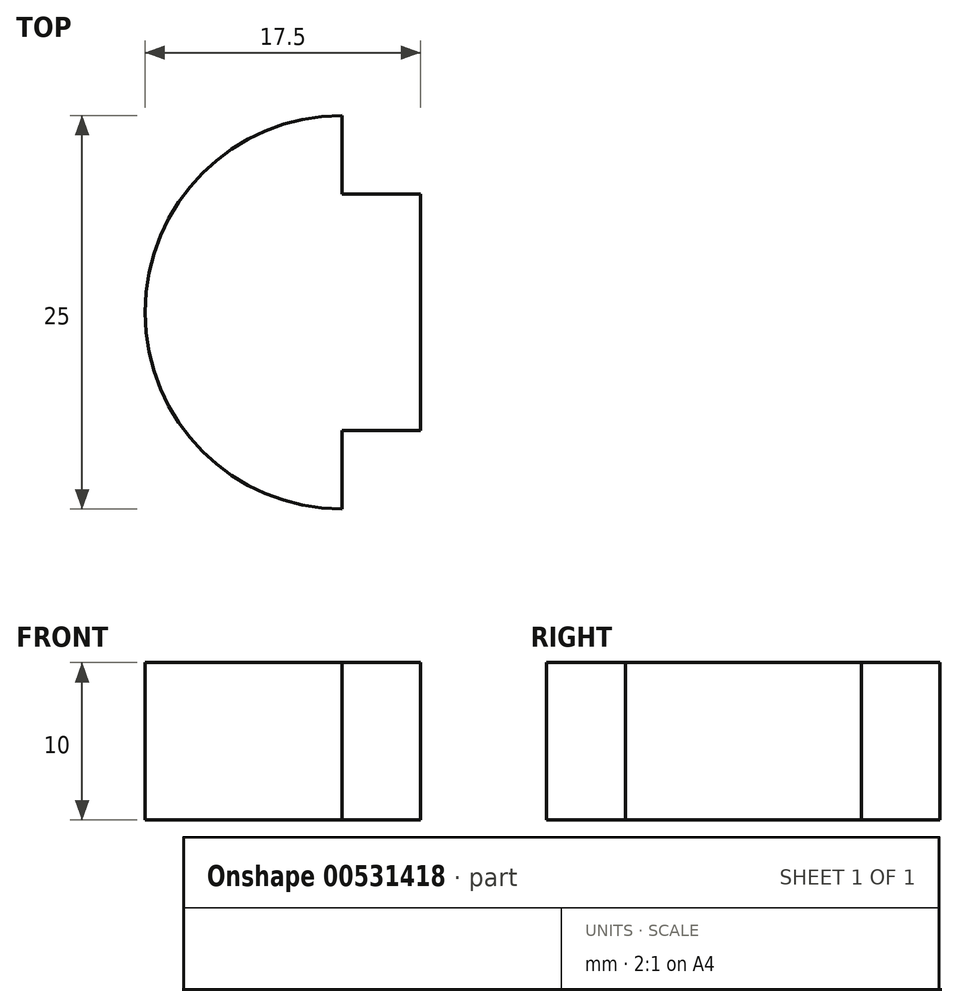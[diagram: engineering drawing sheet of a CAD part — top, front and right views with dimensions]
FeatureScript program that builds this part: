
annotation { "Feature Type Name" : "Feature", "Feature Type Description" : "" }
export const myFeature = defineFeature(function(context is Context, id is Id, definition is map)
    precondition{}
    {
        {
            var Q0;
            Q0=qCreatedBy(makeId("Top.planeOp"),FACE);
            var sketch = newSketch(context, id + "F0", { "sketchPlane" : qUnion([Q0])});
            skArc(sketch, "E0", {"start": v(0, 12.5) * mm, "mid": v(-12.5, 0) * mm, "end": v(0, -12.5) * mm});
            skLineSegment(sketch, "E1", {"start": v(0, 12.5) * mm, "end": v(0, 7.5) * mm});
            skLineSegment(sketch, "E2", {"start": v(0, 7.5) * mm, "end": v(5, 7.5) * mm});
            skLineSegment(sketch, "E3", {"start": v(5, 7.5) * mm, "end": v(5, -7.5) * mm});
            skLineSegment(sketch, "E4", {"start": v(5, -7.5) * mm, "end": v(0, -7.5) * mm});
            skLineSegment(sketch, "E5", {"start": v(0, -7.5) * mm, "end": v(0, -12.5) * mm});
            skSolve(sketch);
        }
        {
            var Q0;
            Q0 = qSketchRegion(id + "F0", true);
            extrude(context, id + "F1", {"entities" : qUnion([Q0]), "depth" : 10 * mm, "offsetDistance" : 25 * mm});
        }
    });
